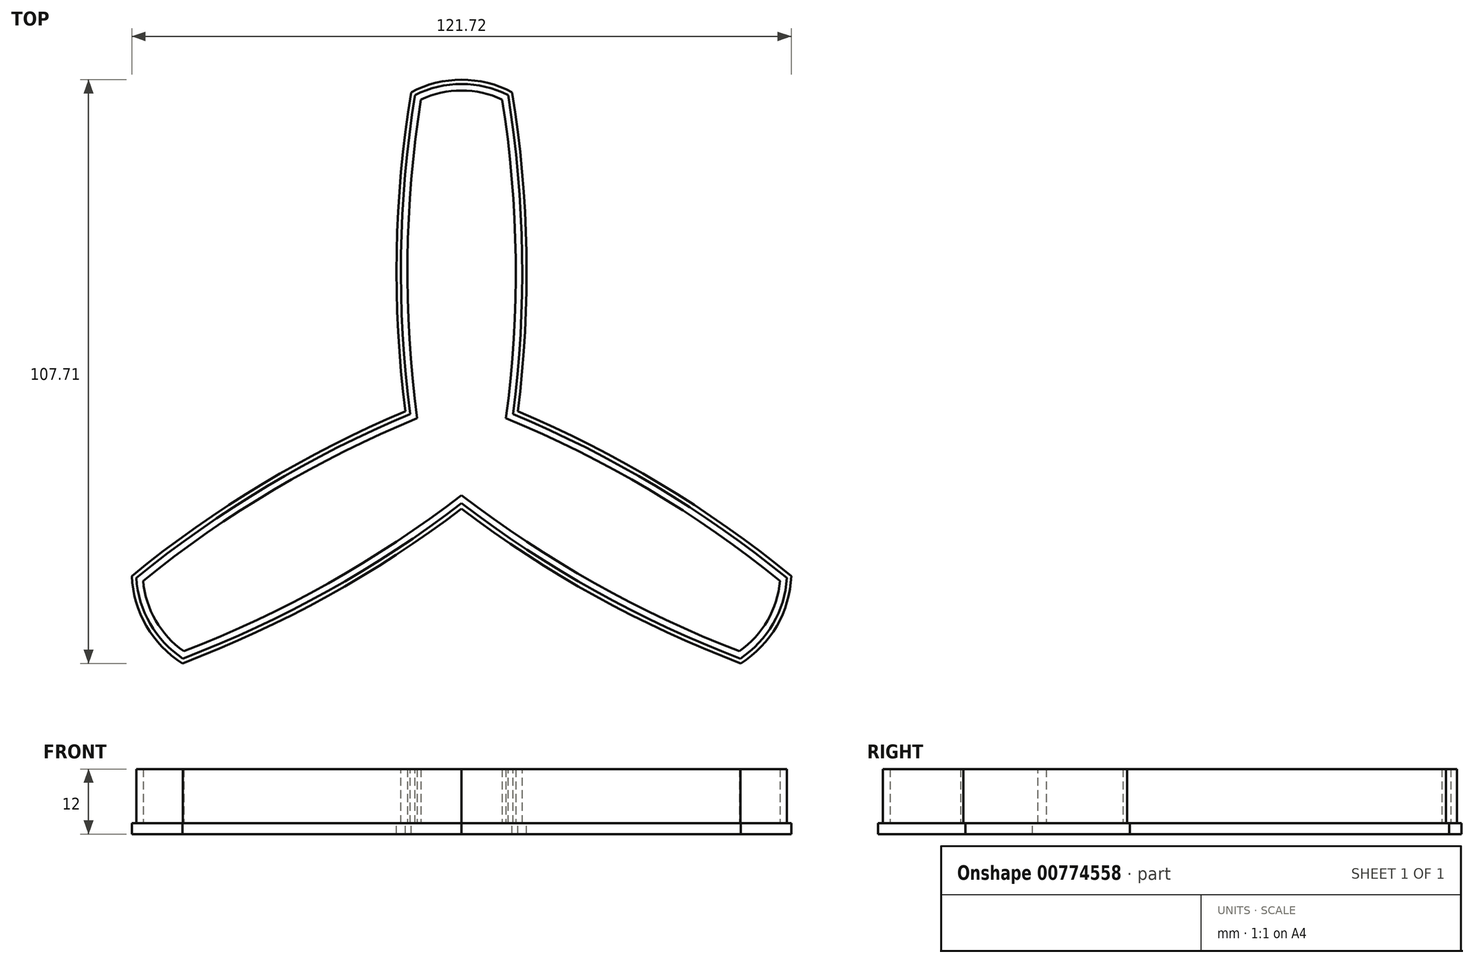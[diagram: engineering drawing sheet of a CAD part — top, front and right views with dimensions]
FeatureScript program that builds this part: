
annotation { "Feature Type Name" : "Feature", "Feature Type Description" : "" }
export const myFeature = defineFeature(function(context is Context, id is Id, definition is map)
    precondition{}
    {
        {
            var Q0;
            Q0=qCreatedBy(makeId("Top.planeOp"),FACE);
            var sketch = newSketch(context, id + "F0", { "sketchPlane" : qUnion([Q0])});
            skCircle(sketch, "E0", {"center": v(0, 0) * mm, "radius": 7.5 * mm});
            skCircle(sketch, "E1", {"center": v(0, 0) * mm, "radius": 64 * mm, "construction": true});
            skLineSegment(sketch, "E2", {"start": v(0, 64) * mm, "end": v(0, 0) * mm, "construction": true});
            skPoint(sketch, "E3", {"position": v(7.5, 63.56) * mm});
            skPoint(sketch, "E4.MirrorP", {"position": v(-7.5, 63.56) * mm});
            skArc(sketch, "E5", {"start": v(7.5, 63.56) * mm, "mid": v(0, 65.2) * mm, "end": v(-7.5, 63.56) * mm});
            skArc(sketch, "E6", {"start": v(8.2, 4.73) * mm, "mid": v(9.99, 34.17) * mm, "end": v(7.5, 63.56) * mm});
            skArc(sketch, "E7.MirrorCS", {"start": v(-8.2, 4.73) * mm, "mid": v(-9.99, 34.17) * mm, "end": v(-7.5, 63.56) * mm});
            skLineSegment(sketch, "E8", {"start": v(-71.33, 41.18) * mm, "end": v(-10.37, 5.99) * mm, "construction": true});
            skLineSegment(sketch, "E9", {"start": v(67.42, 38.92) * mm, "end": v(-67.66, -39.06) * mm, "construction": true});
            skPoint(sketch, "E10.MirrorP", {"position": v(-58.8, -25.28) * mm});
            skArc(sketch, "E11.MirrorCS", {"start": v(-51.3, -38.27) * mm, "mid": v(-56.46, -32.6) * mm, "end": v(-58.8, -25.28) * mm});
            skArc(sketch, "E12.MirrorCS", {"start": v(-8.2, 4.73) * mm, "mid": v(-34.58, -8.44) * mm, "end": v(-58.8, -25.28) * mm});
            skArc(sketch, "E13.MirrorCS", {"start": v(0, -9.46) * mm, "mid": v(-24.6, -25.73) * mm, "end": v(-51.3, -38.27) * mm});
            skArc(sketch, "E14.MirrorCS", {"start": v(0, -9.46) * mm, "mid": v(24.6, -25.73) * mm, "end": v(51.3, -38.27) * mm});
            skArc(sketch, "E15.MirrorCS", {"start": v(8.2, 4.73) * mm, "mid": v(34.58, -8.44) * mm, "end": v(58.8, -25.28) * mm});
            skArc(sketch, "E16.MirrorCS", {"start": v(58.8, -25.28) * mm, "mid": v(56.46, -32.6) * mm, "end": v(51.3, -38.27) * mm});
            skArc(sketch, "E17.0", {"start": v(10.37, 5.99) * mm, "mid": v(11.97, 35.48) * mm, "end": v(9.31, 64.9) * mm});
            skArc(sketch, "E17.1", {"start": v(9.31, 64.9) * mm, "mid": v(0, 67.2) * mm, "end": v(-9.31, 64.9) * mm});
            skArc(sketch, "E17.2", {"start": v(-10.37, 5.99) * mm, "mid": v(-11.97, 35.48) * mm, "end": v(-9.31, 64.9) * mm});
            skArc(sketch, "E18.MirrorCS", {"start": v(10.37, 5.99) * mm, "mid": v(36.71, -7.38) * mm, "end": v(60.86, -24.38) * mm});
            skArc(sketch, "E19.MirrorCS", {"start": v(0, -11.98) * mm, "mid": v(24.74, -28.1) * mm, "end": v(51.55, -40.51) * mm});
            skArc(sketch, "E20.MirrorCS", {"start": v(60.86, -24.38) * mm, "mid": v(58.2, -33.6) * mm, "end": v(51.55, -40.51) * mm});
            skArc(sketch, "E21.MirrorCS", {"start": v(0, -11.98) * mm, "mid": v(-24.74, -28.1) * mm, "end": v(-51.55, -40.51) * mm});
            skArc(sketch, "E22.MirrorCS", {"start": v(-10.37, 5.99) * mm, "mid": v(-36.71, -7.38) * mm, "end": v(-60.86, -24.38) * mm});
            skArc(sketch, "E23.MirrorCS", {"start": v(-51.55, -40.51) * mm, "mid": v(-58.2, -33.6) * mm, "end": v(-60.86, -24.38) * mm});
            skPoint(sketch, "E24.orphan", {"position": v(-16.32, 3.38) * mm});
            skPoint(sketch, "E25.orphan", {"position": v(-3.75, 6.5) * mm});
            skPoint(sketch, "E26.orphan", {"position": v(-7.5, 0) * mm});
            skPoint(sketch, "E27.orphan", {"position": v(-11.09, 12.45) * mm});
            skLineSegment(sketch, "E28.trimOffspring", {"start": v(-8.2, 4.73) * mm, "end": v(57.36, -33.12) * mm, "construction": true});
            skPoint(sketch, "E29.orphan", {"position": v(5.24, -15.83) * mm});
            skPoint(sketch, "E30.orphan", {"position": v(-3.75, -6.5) * mm});
            skPoint(sketch, "E31.orphan", {"position": v(3.75, -6.5) * mm});
            skPoint(sketch, "E32.orphan", {"position": v(-5.24, -15.83) * mm});
            skPoint(sketch, "E33.orphan", {"position": v(3.75, 6.5) * mm});
            skPoint(sketch, "E34.orphan", {"position": v(16.32, 3.38) * mm});
            skPoint(sketch, "E35.orphan", {"position": v(7.5, 0) * mm});
            skPoint(sketch, "E36.orphan", {"position": v(11.09, 12.45) * mm});
            skSolve(sketch);
        }
        {
            var Q0;
            Q0=makeQuery(id+"F0.imprint","IMPRINT",FACE,{"disambiguationData":[TD([[makeQuery(id+"F0.imprint","IMPRINT",EDGE,{"derivedFrom":sQuery(id+"F0.wireOp",EDGE,"E5")}),-1.0]])]});
            extrude(context, id + "F1", {"entities" : qUnion([Q0]), "depth" : 10 * mm, "offsetDistance" : 25 * mm});
        }
        {
            var Q0;
            Q0=makeQuery(id+"F1.opExtrude","CAP_FACE",FACE,{"disambiguationData":[OSD([sQuery(id+"F0.wireOp",EDGE,"E5"),sQuery(id+"F0.wireOp",EDGE,"E6"),sQuery(id+"F0.wireOp",EDGE,"E7.MirrorCS"),sQuery(id+"F0.wireOp",EDGE,"E11.MirrorCS"),sQuery(id+"F0.wireOp",EDGE,"E12.MirrorCS"),sQuery(id+"F0.wireOp",EDGE,"E13.MirrorCS"),sQuery(id+"F0.wireOp",EDGE,"E14.MirrorCS"),sQuery(id+"F0.wireOp",EDGE,"E15.MirrorCS"),sQuery(id+"F0.wireOp",EDGE,"E16.MirrorCS"),sQuery(id+"F0.wireOp",EDGE,"E17.0"),sQuery(id+"F0.wireOp",EDGE,"E17.1"),sQuery(id+"F0.wireOp",EDGE,"E17.2"),sQuery(id+"F0.wireOp",EDGE,"E18.MirrorCS"),sQuery(id+"F0.wireOp",EDGE,"E19.MirrorCS"),sQuery(id+"F0.wireOp",EDGE,"E20.MirrorCS"),sQuery(id+"F0.wireOp",EDGE,"E21.MirrorCS"),sQuery(id+"F0.wireOp",EDGE,"E22.MirrorCS"),sQuery(id+"F0.wireOp",EDGE,"E23.MirrorCS")])],"isStart":false});
            var sketch = newSketch(context, id + "F2", { "sketchPlane" : qUnion([Q0])});
            skArc(sketch, "E37.0", {"start": v(-9.5, 5.49) * mm, "mid": v(-11.18, 34.96) * mm, "end": v(-8.59, 64.37) * mm});
            skArc(sketch, "E37.1", {"start": v(8.59, 64.37) * mm, "mid": v(0, 66.4) * mm, "end": v(-8.59, 64.37) * mm});
            skArc(sketch, "E37.2", {"start": v(-9.5, 5.49) * mm, "mid": v(-35.86, -7.8) * mm, "end": v(-60.04, -24.75) * mm});
            skArc(sketch, "E37.3", {"start": v(9.5, 5.49) * mm, "mid": v(11.18, 34.96) * mm, "end": v(8.59, 64.37) * mm});
            skArc(sketch, "E37.4", {"start": v(9.5, 5.49) * mm, "mid": v(35.86, -7.8) * mm, "end": v(60.04, -24.75) * mm});
            skArc(sketch, "E37.5", {"start": v(-51.45, -39.62) * mm, "mid": v(-57.5, -33.2) * mm, "end": v(-60.04, -24.75) * mm});
            skArc(sketch, "E37.6", {"start": v(0, -10.97) * mm, "mid": v(-24.69, -27.16) * mm, "end": v(-51.45, -39.62) * mm});
            skArc(sketch, "E37.7", {"start": v(0, -10.97) * mm, "mid": v(24.69, -27.16) * mm, "end": v(51.45, -39.62) * mm});
            skArc(sketch, "E37.8", {"start": v(60.04, -24.75) * mm, "mid": v(57.5, -33.2) * mm, "end": v(51.45, -39.62) * mm});
            skSolve(sketch);
        }
        {
            var Q0;
            Q0=makeQuery(id+"F2.imprint","IMPRINT",FACE,{"disambiguationData":[TD([[makeQuery(id+"F2.imprint","IMPRINT",EDGE,{"derivedFrom":sQuery(id+"F2.wireOp",EDGE,"E37.0")}),-1.0]])]});
            extrude(context, id + "F3", {"entities" : qUnion([Q0]), "operationType" : NewBodyOperationType.REMOVE, "oppositeDirection" : true, "depth" : 10 * mm, "offsetDistance" : 25 * mm});
        }
        {
            var Q0;
            Q0 = qSketchRegion(id + "F0", true);
            var Q1;
            Q1=makeQuery(id+"F0.imprint","IMPRINT",FACE,{"disambiguationData":[TD([[makeQuery(id+"F0.imprint","IMPRINT",EDGE,{"derivedFrom":sQuery(id+"F0.wireOp",EDGE,"E0")}),-1.0]])]});
            var Q2;
            Q2=makeQuery(id+"F0.imprint","IMPRINT",FACE,{"disambiguationData":[TD([[makeQuery(id+"F0.imprint","IMPRINT",EDGE,{"derivedFrom":sQuery(id+"F0.wireOp",EDGE,"E0")}),1.0]])]});
            extrude(context, id + "F4", {"entities" : qUnion([Q0, Q1, Q2]), "operationType" : NewBodyOperationType.ADD, "oppositeDirection" : true, "depth" : 2 * mm, "offsetDistance" : 25 * mm});
        }
    });
